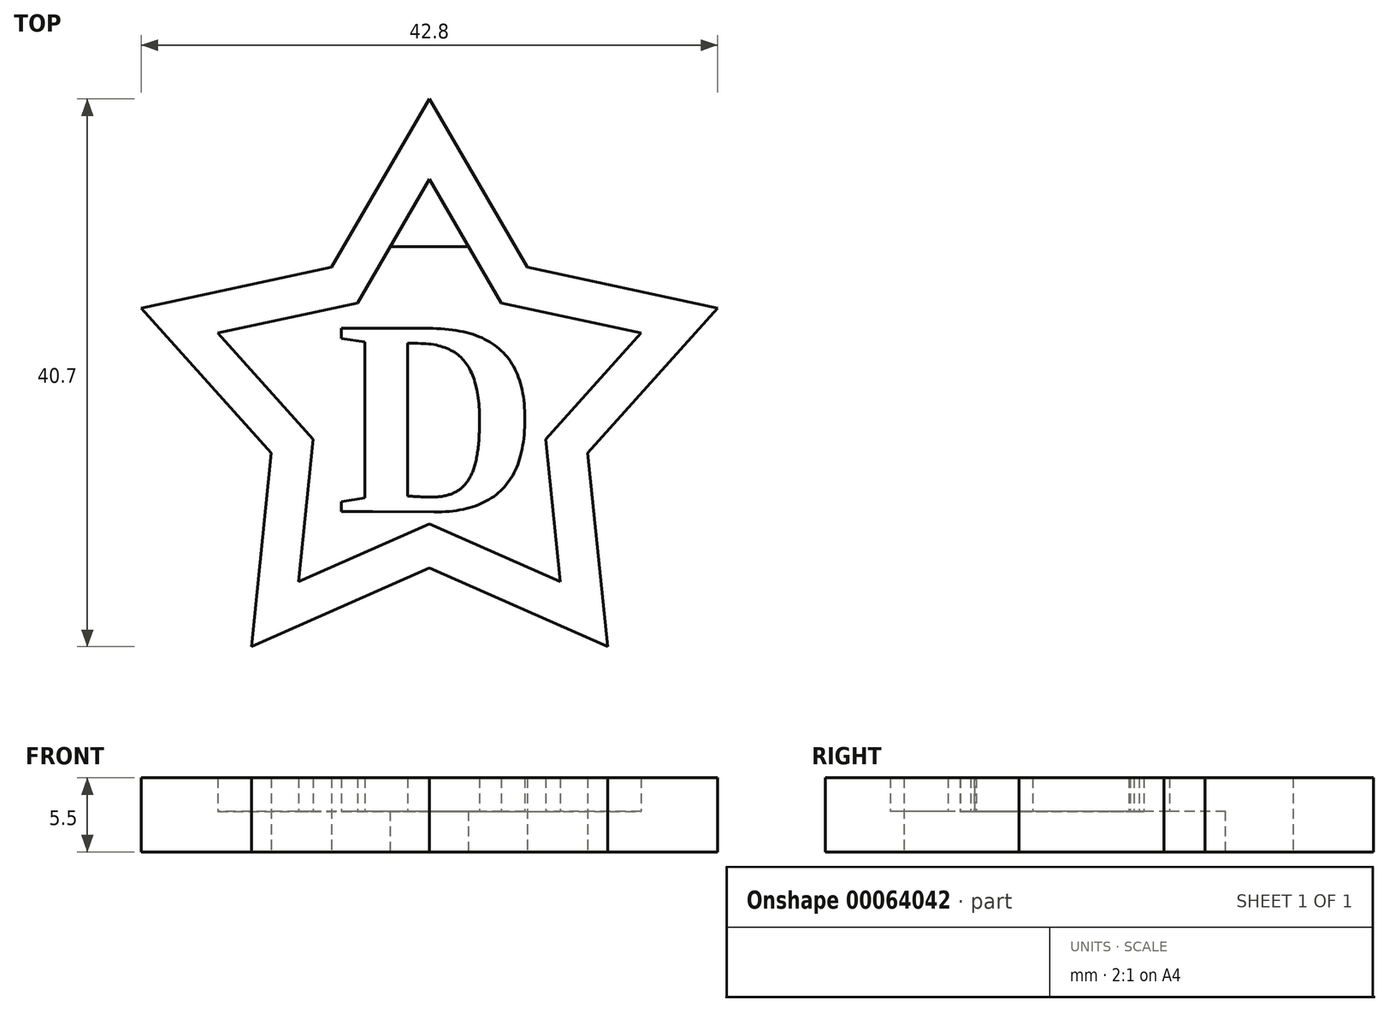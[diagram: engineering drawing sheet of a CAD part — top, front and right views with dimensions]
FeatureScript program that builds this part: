
annotation { "Feature Type Name" : "Feature", "Feature Type Description" : "" }
export const myFeature = defineFeature(function(context is Context, id is Id, definition is map)
    precondition{}
    {
        {
            var Q0;
            Q0=qCreatedBy(makeId("Top.planeOp"),FACE);
            var sketch = newSketch(context, id + "F0", { "sketchPlane" : qUnion([Q0])});
            skCircle(sketch, "E0.cCircle", {"center": v(0, 0) * mm, "radius": 10 * mm, "construction": true});
            skLineSegment(sketch, "E0.0", {"start": v(-7.27, 10) * mm, "end": v(7.27, 10) * mm, "construction": true});
            skLineSegment(sketch, "E0.1", {"start": v(7.27, 10) * mm, "end": v(11.76, -3.82) * mm, "construction": true});
            skLineSegment(sketch, "E0.2", {"start": v(11.76, -3.82) * mm, "end": v(0, -12.36) * mm, "construction": true});
            skLineSegment(sketch, "E0.3", {"start": v(0, -12.36) * mm, "end": v(-11.76, -3.82) * mm, "construction": true});
            skLineSegment(sketch, "E0.4", {"start": v(-11.76, -3.82) * mm, "end": v(-7.27, 10) * mm, "construction": true});
            skPoint(sketch, "E0.0.midPoint", {"position": v(0, 10) * mm});
            skCircle(sketch, "E1", {"center": v(0, 0) * mm, "radius": 22.5 * mm, "construction": true});
            skLineSegment(sketch, "E2", {"start": v(0, -12.36) * mm, "end": v(-13.23, -18.2) * mm});
            skLineSegment(sketch, "E3", {"start": v(-13.23, -18.2) * mm, "end": v(-11.76, -3.82) * mm});
            skLineSegment(sketch, "E4", {"start": v(-11.76, -3.82) * mm, "end": v(-21.4, 6.95) * mm});
            skLineSegment(sketch, "E5", {"start": v(-21.4, 6.95) * mm, "end": v(-7.27, 10) * mm});
            skLineSegment(sketch, "E6", {"start": v(-7.27, 10) * mm, "end": v(0, 22.5) * mm});
            skLineSegment(sketch, "E7", {"start": v(0, 22.5) * mm, "end": v(7.27, 10) * mm});
            skLineSegment(sketch, "E8", {"start": v(7.27, 10) * mm, "end": v(21.4, 6.95) * mm});
            skLineSegment(sketch, "E9", {"start": v(21.4, 6.95) * mm, "end": v(11.76, -3.82) * mm});
            skLineSegment(sketch, "E10", {"start": v(11.76, -3.82) * mm, "end": v(13.23, -18.2) * mm});
            skLineSegment(sketch, "E11", {"start": v(0, -12.36) * mm, "end": v(13.23, -18.2) * mm});
            skSolve(sketch);
        }
        {
            var Q0;
            Q0=makeQuery(id+"F0.imprint","IMPRINT",FACE,{"disambiguationData":[TD([[makeQuery(id+"F0.imprint","IMPRINT",EDGE,{"derivedFrom":sQuery(id+"F0.wireOp",EDGE,"E2")}),-1.0]])]});
            extrude(context, id + "F1", {"entities" : qUnion([Q0]), "depth" : 5.5 * mm});
        }
        {
            var Q0;
            Q0=makeQuery(id+"F1.opExtrude","CAP_FACE",FACE,{"disambiguationData":[OSD([sQuery(id+"F0.wireOp",EDGE,"E2"),sQuery(id+"F0.wireOp",EDGE,"E3"),sQuery(id+"F0.wireOp",EDGE,"E4"),sQuery(id+"F0.wireOp",EDGE,"E5"),sQuery(id+"F0.wireOp",EDGE,"E6"),sQuery(id+"F0.wireOp",EDGE,"E7"),sQuery(id+"F0.wireOp",EDGE,"E8"),sQuery(id+"F0.wireOp",EDGE,"E9"),sQuery(id+"F0.wireOp",EDGE,"E10"),sQuery(id+"F0.wireOp",EDGE,"E11")])],"isStart":false});
            shell(context, id + "F2", {"entities" : qUnion([Q0]), "thickness" : 3 * mm});
        }
        {
            var Q0;
            Q0=makeQuery(id+"F2.opShell","OFFSET_FACE",FACE,{"disambiguationData":[OSD([sQuery(id+"F0.wireOp",EDGE,"E2"),sQuery(id+"F0.wireOp",EDGE,"E3"),sQuery(id+"F0.wireOp",EDGE,"E4"),sQuery(id+"F0.wireOp",EDGE,"E5"),sQuery(id+"F0.wireOp",EDGE,"E6"),sQuery(id+"F0.wireOp",EDGE,"E7"),sQuery(id+"F0.wireOp",EDGE,"E8"),sQuery(id+"F0.wireOp",EDGE,"E9"),sQuery(id+"F0.wireOp",EDGE,"E10"),sQuery(id+"F0.wireOp",EDGE,"E11")])]});
            var sketch = newSketch(context, id + "F3", { "sketchPlane" : qUnion([Q0])});
            skLineSegment(sketch, "E12", {"start": v(-2.9, 11.53) * mm, "end": v(2.9, 11.53) * mm});
            skLineSegment(sketch, "E13", {"start": v(2.9, 11.53) * mm, "end": v(0, 16.53) * mm});
            skLineSegment(sketch, "E14", {"start": v(0, 16.53) * mm, "end": v(-2.9, 11.53) * mm});
            skSolve(sketch);
        }
        {
            var Q0;
            {var subQ0=sQuery(id+"F3.wireOp",EDGE,"ukyzmsq6-fGPh-QabO-RgtZ-QhB85LGewBzE");var subQ1=sQuery(id+"F0.wireOp",EDGE,"E6");var subQ2=makeQuery(id+"F3.imprint","INTERSECT",VERTEX,{"derivedFrom":[makeQuery(id+"F2.opShell","OFFSET_EDGE",EDGE,{"disambiguationData":[OSD([subQ1]),TDD([makeQuery(id+"F1.opExtrude","CAP_EDGE",EDGE,{"disambiguationData":[OSD([subQ1])],"isStart":true})])]}),subQ0]});Q0=makeQuery(id+"F3.imprint","IMPRINT",FACE,{"disambiguationData":[TD([[makeQuery(id+"F3.imprint","IMPRINT",EDGE,{"disambiguationData":[TD([[subQ2,1.0]])],"derivedFrom":subQ0}),1.0]])]});}
            var Q1;
            Q1=makeQuery(id+"F3.imprint","IMPRINT",FACE,{"disambiguationData":[TD([[makeQuery(id+"F3.imprint","IMPRINT",EDGE,{"derivedFrom":sQuery(id+"F3.wireOp",EDGE,"E12")}),1.0]])]});
            extrude(context, id + "F4", {"entities" : qUnion([Q0, Q1]), "operationType" : NewBodyOperationType.REMOVE, "endBound" : BoundingType.UP_TO_NEXT, "oppositeDirection" : true, "depth" : 25 * mm});
        }
        {
            var Q0;
            Q0=makeQuery(id+"F2.opShell","OFFSET_FACE",FACE,{"disambiguationData":[OSD([sQuery(id+"F0.wireOp",EDGE,"E2"),sQuery(id+"F0.wireOp",EDGE,"E3"),sQuery(id+"F0.wireOp",EDGE,"E4"),sQuery(id+"F0.wireOp",EDGE,"E5"),sQuery(id+"F0.wireOp",EDGE,"E6"),sQuery(id+"F0.wireOp",EDGE,"E7"),sQuery(id+"F0.wireOp",EDGE,"E8"),sQuery(id+"F0.wireOp",EDGE,"E9"),sQuery(id+"F0.wireOp",EDGE,"E10"),sQuery(id+"F0.wireOp",EDGE,"E11")])]});
            var sketch = newSketch(context, id + "F5", { "sketchPlane" : qUnion([Q0])});
            skText(sketch, "E15", { "text": "D", "fontName": "Tinos-Bold.ttf"});
            const initialGuessF5  = {"E15": [-0.00691, -0.00816, 1, 0, 0.01497]};
            skSetInitialGuess(sketch, initialGuessF5);
            skSolve(sketch);
        }
        {
            var Q0;
            Q0=makeQuery(id+"F5.imprint","IMPRINT",FACE,{"disambiguationData":[TD([[makeQuery(id+"F5.imprint","IMPRINT",EDGE,{"derivedFrom":sQuery(id+"F5.wireOp",EDGE,"E15.sketch_text.stroke-0")}),-1.0]])]});
            extrude(context, id + "F6", {"entities" : qUnion([Q0]), "operationType" : NewBodyOperationType.ADD, "depth" : 2.5 * mm});
        }
    });
